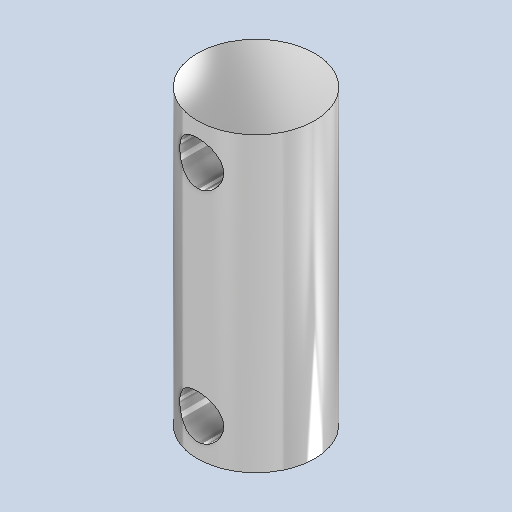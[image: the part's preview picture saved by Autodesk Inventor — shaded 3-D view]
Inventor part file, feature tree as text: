
AUTODESK INVENTOR PART (.ipt)
format: ipt  version: 2025.1 (Build 291241000, 241)  size: 141,824 bytes
history: native  units: mm
features: other x3, sketch x2, extrude x1, plane x1, hole x1, reference x1
ambient origin geometry x8: Origin, YZ Plane, XZ Plane, XY Plane, X Axis, Y Axis, Z Axis, Center Point
bodies: Solid1 (feature_tree)
feature tree (9):
  extrude  "Extrusion1"  Depth=19.0mm
  plane  "Work Plane1"
  hole  "Hole1"  [1 undecoded]
  sketch  "Sketch1"  dims[d0=20.0mm d1=0.0mm d2=19.0mm]
  reference  "Reference1"
  sketch  "Sketch2"  dims[d3=2.5mm d4=2.5mm d5=3.0mm d6=6.0mm d7=4.0mm d8=2.0mm d9=90.0deg d10=8.0mm d11=20.594885mm]
  parser-record x1  (decoder bookkeeping rows leaked as tree rows — omitted from the tree; the rows remain in map.json)
  other  "Welle.iam"
  other  "201 part 3:2"
note: 1 required parameter value undecoded (feature->parameter linkage not recoverable at this tier; creation-order binding heuristic only, values carry confidence <= 0.55)
note: 1 file-system path scrubbed to <path> (originals preserved in map.json)
